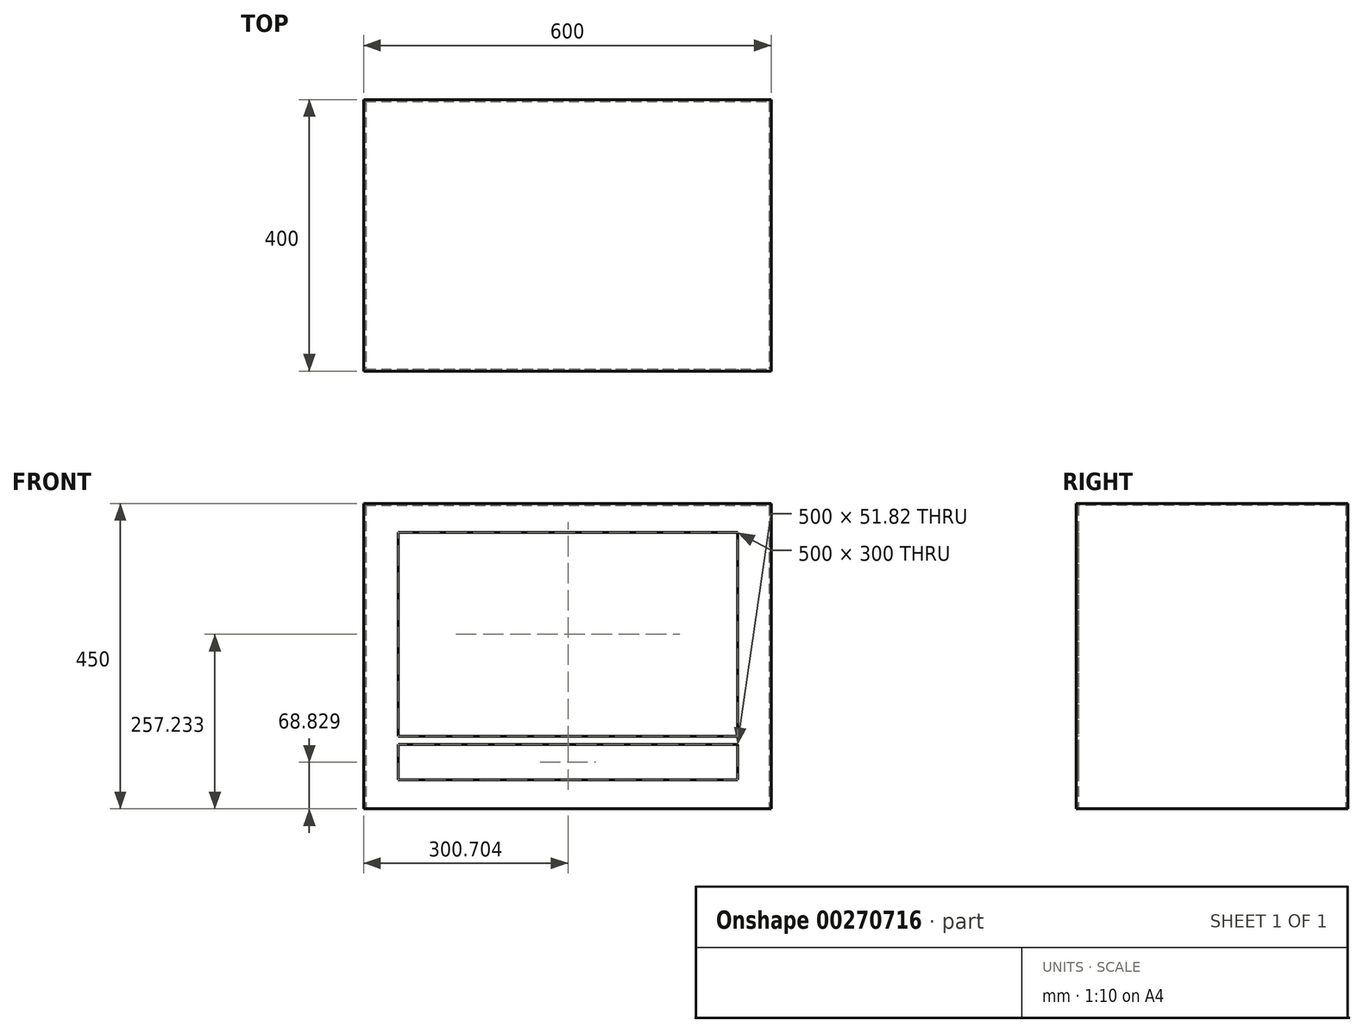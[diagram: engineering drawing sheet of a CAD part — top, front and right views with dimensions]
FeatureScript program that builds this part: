
annotation { "Feature Type Name" : "Feature", "Feature Type Description" : "" }
export const myFeature = defineFeature(function(context is Context, id is Id, definition is map)
    precondition{}
    {
        {
            var Q0;
            Q0=qCreatedBy(makeId("Front.planeOp"),FACE);
            var sketch = newSketch(context, id + "F0", { "sketchPlane" : qUnion([Q0])});
            skLineSegment(sketch, "E0.bottom", {"start": v(-300, 225) * mm, "end": v(300, 225) * mm});
            skLineSegment(sketch, "E0.top", {"start": v(-300, -225) * mm, "end": v(300, -225) * mm});
            skLineSegment(sketch, "E0.left", {"start": v(-300, 225) * mm, "end": v(-300, -225) * mm});
            skLineSegment(sketch, "E0.right", {"start": v(300, 225) * mm, "end": v(300, -225) * mm});
            skPoint(sketch, "E0.middle", {"position": v(0, 0) * mm});
            skLineSegment(sketch, "E1.bottom", {"start": v(250.7, 182.23) * mm, "end": v(-249.3, 182.23) * mm});
            skLineSegment(sketch, "E1.top", {"start": v(250.7, -117.77) * mm, "end": v(-249.3, -117.77) * mm});
            skLineSegment(sketch, "E1.left", {"start": v(250.7, 182.23) * mm, "end": v(250.7, -117.77) * mm});
            skLineSegment(sketch, "E1.right", {"start": v(-249.3, 182.23) * mm, "end": v(-249.3, -117.77) * mm});
            skLineSegment(sketch, "E2.bottom", {"start": v(-249.3, -130.26) * mm, "end": v(250.7, -130.26) * mm});
            skLineSegment(sketch, "E2.top", {"start": v(-249.3, -182.08) * mm, "end": v(250.7, -182.08) * mm});
            skLineSegment(sketch, "E2.left", {"start": v(-249.3, -130.26) * mm, "end": v(-249.3, -182.08) * mm});
            skLineSegment(sketch, "E2.right", {"start": v(250.7, -130.26) * mm, "end": v(250.7, -182.08) * mm});
            skSolve(sketch);
        }
        {
            var Q0;
            Q0=makeQuery(id+"F0.imprint","IMPRINT",FACE,{"disambiguationData":[TD([[makeQuery(id+"F0.imprint","IMPRINT",EDGE,{"derivedFrom":sQuery(id+"F0.wireOp",EDGE,"E0.bottom")}),-1.0]])]});
            var Q1;
            Q1=makeQuery(id+"F0.imprint","IMPRINT",FACE,{"disambiguationData":[TD([[makeQuery(id+"F0.imprint","IMPRINT",EDGE,{"derivedFrom":sQuery(id+"F0.wireOp",EDGE,"E1.bottom")}),1.0]])]});
            var Q2;
            Q2=makeQuery(id+"F0.imprint","IMPRINT",FACE,{"disambiguationData":[TD([[makeQuery(id+"F0.imprint","IMPRINT",EDGE,{"derivedFrom":sQuery(id+"F0.wireOp",EDGE,"E2.bottom")}),-1.0]])]});
            extrude(context, id + "F1", {"entities" : qUnion([Q0, Q1, Q2]), "oppositeDirection" : true, "depth" : 400 * mm});
        }
        {
            var Q0;
            Q0=makeQuery(id+"F1.opExtrude","SWEPT_FACE",FACE,{"disambiguationData":[OSD([sQuery(id+"F0.wireOp",EDGE,"E0.top")])]});
            shell(context, id + "F2", {"entities" : qUnion([Q0]), "thickness" : 3 * mm});
        }
        {
            var Q0;
            Q0=makeQuery(id+"F0.imprint","IMPRINT",FACE,{"disambiguationData":[TD([[makeQuery(id+"F0.imprint","IMPRINT",EDGE,{"derivedFrom":sQuery(id+"F0.wireOp",EDGE,"E1.bottom")}),1.0]])]});
            var Q1;
            Q1=makeQuery(id+"F0.imprint","IMPRINT",FACE,{"disambiguationData":[TD([[makeQuery(id+"F0.imprint","IMPRINT",EDGE,{"derivedFrom":sQuery(id+"F0.wireOp",EDGE,"E2.bottom")}),-1.0]])]});
            extrude(context, id + "F3", {"entities" : qUnion([Q0, Q1]), "operationType" : NewBodyOperationType.REMOVE, "oppositeDirection" : true, "depth" : 3 * mm});
        }
    });
